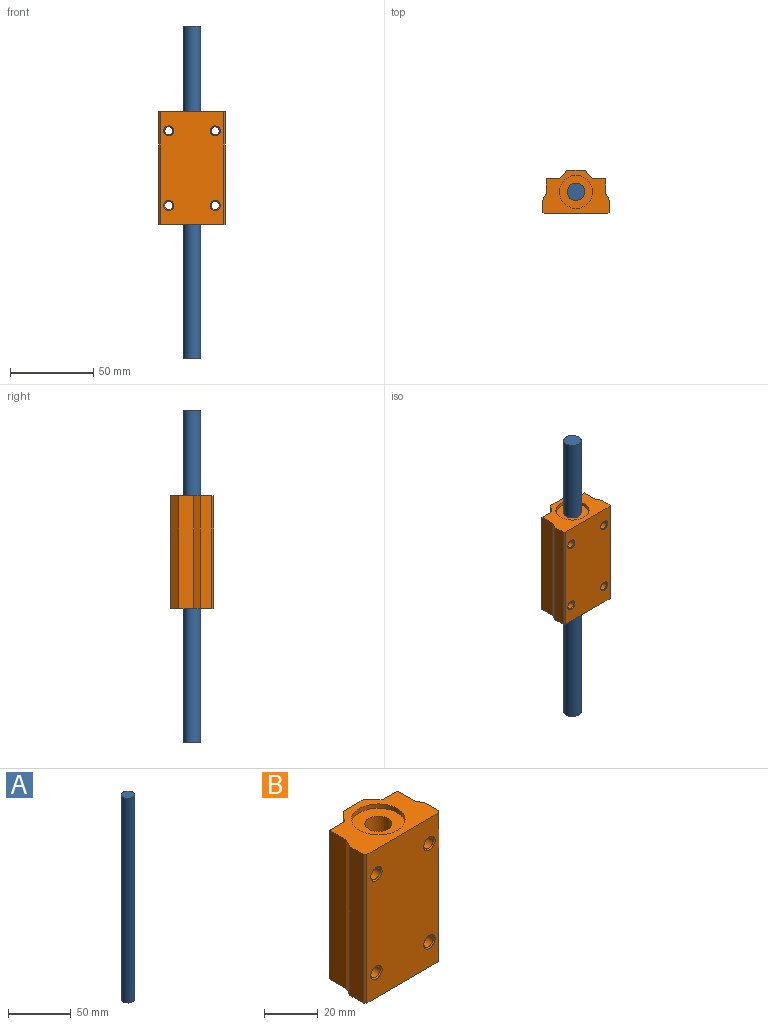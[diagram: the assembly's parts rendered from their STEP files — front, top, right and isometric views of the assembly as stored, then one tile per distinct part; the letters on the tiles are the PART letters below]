
ASSEMBLY  parts=2 mates=1
PART A: 3 faces, bbox 10.5x10.5x200 mm
  f0: cylinder r=5.25mm len=200mm, axis (0,0,-1), area 6597.3mm2, adj f1,f2
  f1: plane 10.5x10.5mm, normal (0,0,1), area 86.6mm2, adj f0
  f2: plane 10.5x10.5mm, normal (0,0,-1), area 86.6mm2, adj f0
PART B: 29 faces, bbox 40x26x68 mm
  f0: plane 68x8mm, normal (0,1,0), area 504.7mm2, adj f6,f7,f16,f17,f21,f22
  f1: plane 68x8mm, normal (0,1,0), area 504.7mm2, adj f9,f10,f16,f17,f23,f24
  f2: plane 68x38mm, normal (0,-1,0), area 2470.9mm2, adj f13,f14,f16,f17,f25,f26,f27,f28
  f3: cylinder r=10mm len=20mm, axis (0,0,-1), area 125.7mm2, adj f16,f19
  f4: plane 68x7mm, normal (1,0,0), area 476mm2, adj f5,f14,f16,f17
  f5: plane 68x4mm, normal (0.89,0.45,0), area 304.1mm2, adj f4,f6,f16,f17
  f6: plane 68x9mm, normal (1,0,0), area 612mm2, adj f0,f5,f16,f17
  f7: plane 68x5mm, normal (0.74,0.67,0), area 457.4mm2, adj f0,f8,f16,f17
  f8: plane 68x11mm, normal (0,1,0), area 748mm2, adj f7,f9,f16,f17
  f9: plane 68x5mm, normal (-0.74,0.67,0), area 457.4mm2, adj f1,f8,f16,f17
  f10: plane 68x9mm, normal (-1,0,0), area 612mm2, adj f1,f11,f16,f17
  f11: plane 68x4mm, normal (-0.89,0.45,0), area 304.1mm2, adj f10,f12,f16,f17
  f12: plane 68x7mm, normal (-1,0,0), area 476mm2, adj f11,f13,f16,f17
  f13: plane 68x1mm, normal (-0.71,-0.71,0), area 96.2mm2, adj f2,f12,f16,f17
  f14: plane 68x1mm, normal (0.71,-0.71,0), area 96.2mm2, adj f2,f4,f16,f17
  f15: cylinder r=10mm len=20mm, axis (0,0,-1), area 125.7mm2, adj f17,f20
  f16: plane 40x26mm, normal (0,0,1), area 558.3mm2, adj f0,f1,f2,f3,f4,f5,f6,f7
  f17: plane 40x26mm, normal (0,0,-1), area 558.3mm2, adj f0,f1,f2,f4,f5,f6,f7,f8
  f18: cylinder r=5mm len=64mm, axis (0,0,-1), area 2010.6mm2, adj f19,f20
  f19: plane 20x20mm, normal (0,0,1), area 235.6mm2, adj f3,f18
  f20: plane 20x20mm, normal (0,0,-1), area 235.6mm2, adj f15,f18
  f21: cylinder r=2.5mm len=20.5mm, axis (0,1,0), area 322mm2, adj f0,f25
  f22: cylinder r=2.5mm len=20.5mm, axis (0,1,0), area 322mm2, adj f0,f26
  f23: cylinder r=2.5mm len=20.5mm, axis (0,1,0), area 322mm2, adj f1,f27
  f24: cylinder r=2.5mm len=20.5mm, axis (0,1,0), area 322mm2, adj f1,f28
  f25: cone r=3mm half-angle=45deg, axis (0,-1,0), area 12.2mm2, adj f2,f21
  f26: cone r=2.5mm half-angle=45deg, axis (0,-1,0), area 12.2mm2, adj f2,f22
  f27: cone r=3mm half-angle=45deg, axis (0,-1,0), area 12.2mm2, adj f2,f23
  f28: cone r=2.5mm half-angle=45deg, axis (0,-1,0), area 12.2mm2, adj f2,f24
PLACE A t=(25.85,-15.38,-13.46)mm fixed
PLACE B t=(25.85,-15.38,0.89)mm
MATE slider A.f0 <-> B.f3  axis (0,0,-1) through (25.85,-15.38,-13.46)mm
